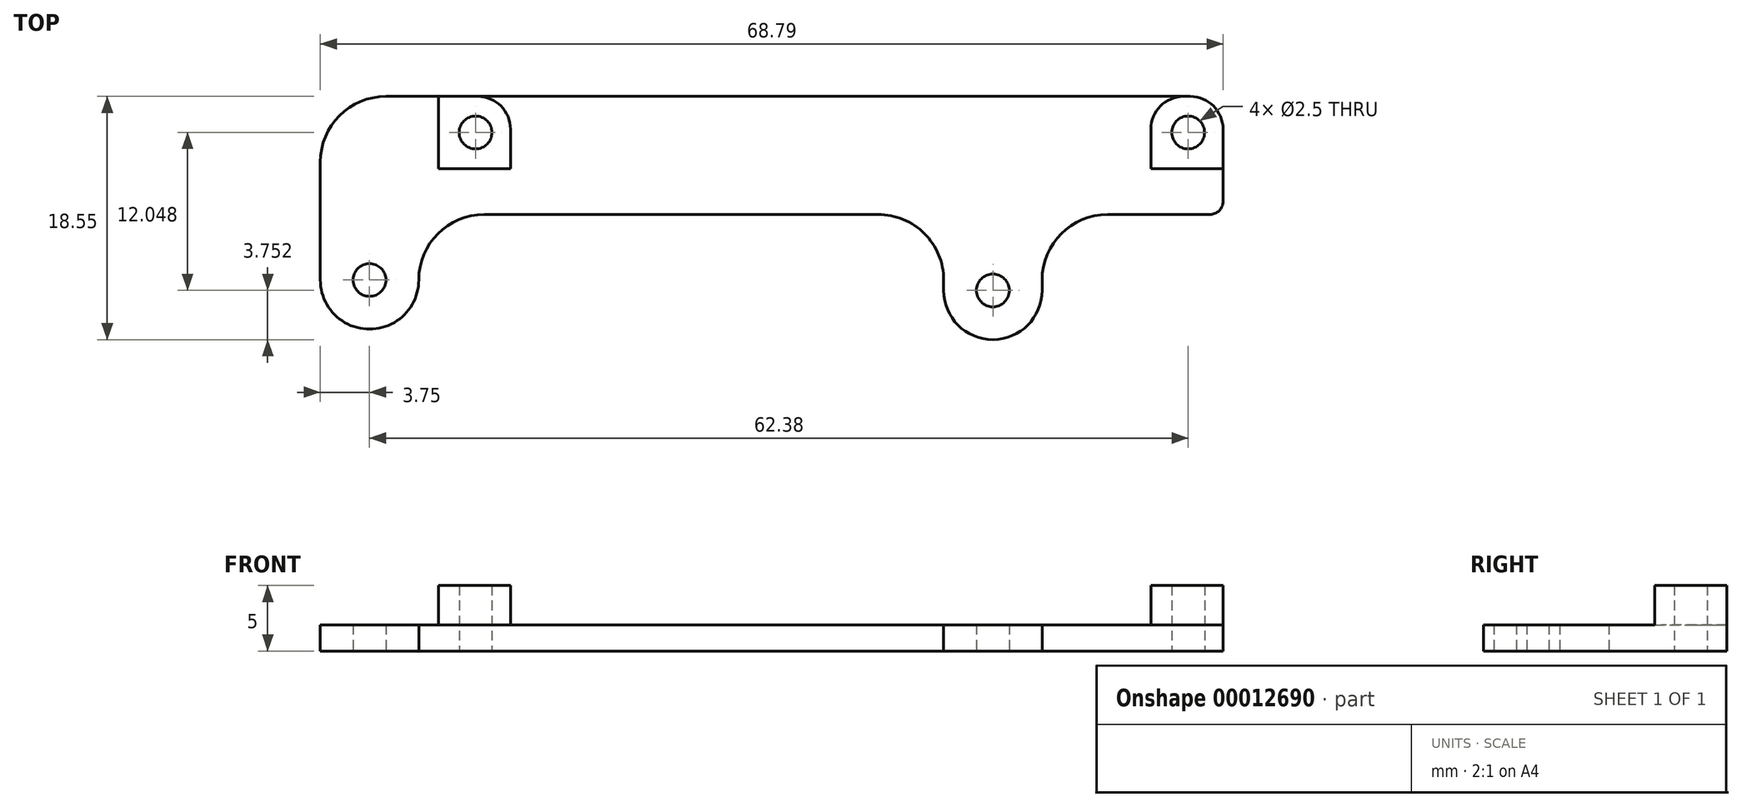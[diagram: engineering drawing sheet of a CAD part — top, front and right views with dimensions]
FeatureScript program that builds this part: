
annotation { "Feature Type Name" : "Feature", "Feature Type Description" : "" }
export const myFeature = defineFeature(function(context is Context, id is Id, definition is map)
    precondition{}
    {
        {
            var Q0;
            Q0=qCreatedBy(makeId("Top.planeOp"),FACE);
            var sketch = newSketch(context, id + "F0", { "sketchPlane" : qUnion([Q0])});
            skCircle(sketch, "E0", {"center": v(4.96, 27.14) * mm, "radius": 1.25 * mm});
            skCircle(sketch, "E1", {"center": v(-42.54, 27.94) * mm, "radius": 1.25 * mm});
            skArc(sketch, "E2.0", {"start": v(-46.3, 27.94) * mm, "mid": v(-42.54, 24.2) * mm, "end": v(-38.8, 27.94) * mm});
            skLineSegment(sketch, "E3", {"start": v(-46.3, 27.94) * mm, "end": v(-46.3, 36.94) * mm});
            skLineSegment(sketch, "E4", {"start": v(-38.8, 27.94) * mm, "end": v(-38.8, 27.94) * mm});
            skLineSegment(sketch, "E5", {"start": v(-33.8, 32.94) * mm, "end": v(-3.8, 32.94) * mm});
            skLineSegment(sketch, "E6", {"start": v(-41.3, 41.94) * mm, "end": v(20, 41.94) * mm});
            skPoint(sketch, "E7.visualSharp", {"position": v(-46.3, 41.94) * mm});
            skArc(sketch, "E7.filletArc", {"start": v(-41.3, 41.94) * mm, "mid": v(-44.83, 40.48) * mm, "end": v(-46.3, 36.94) * mm});
            skPoint(sketch, "E8.visualSharp", {"position": v(8.7, 41.94) * mm});
            skPoint(sketch, "E9.visualSharp", {"position": v(1.2, 32.94) * mm});
            skArc(sketch, "E9.filletArc", {"start": v(1.2, 27.94) * mm, "mid": v(-0.25, 31.48) * mm, "end": v(-3.8, 32.94) * mm});
            skPoint(sketch, "E10.visualSharp", {"position": v(-38.8, 32.94) * mm});
            skArc(sketch, "E10.filletArc", {"start": v(-33.8, 32.94) * mm, "mid": v(-37.33, 31.48) * mm, "end": v(-38.8, 27.94) * mm});
            skLineSegment(sketch, "E11", {"start": v(22.5, 39.44) * mm, "end": v(22.5, 33.93) * mm});
            skLineSegment(sketch, "E12.trimOffspring", {"start": v(13.7, 32.94) * mm, "end": v(21.5, 32.94) * mm});
            skPoint(sketch, "E13.visualSharp", {"position": v(8.7, 32.94) * mm});
            skArc(sketch, "E13.filletArc", {"start": v(13.7, 32.94) * mm, "mid": v(10.17, 31.48) * mm, "end": v(8.7, 27.94) * mm});
            skPoint(sketch, "E14.visualSharp", {"position": v(22.5, 32.94) * mm});
            skArc(sketch, "E14.filletArc", {"start": v(21.5, 32.94) * mm, "mid": v(22.21, 33.23) * mm, "end": v(22.5, 33.93) * mm});
            skPoint(sketch, "E15.visualSharp", {"position": v(22.5, 41.94) * mm});
            skArc(sketch, "E15.filletArc", {"start": v(22.5, 39.44) * mm, "mid": v(21.77, 41.2) * mm, "end": v(20, 41.94) * mm});
            skLineSegment(sketch, "E16", {"start": v(1.2, 27.94) * mm, "end": v(1.2, 27.14) * mm});
            skLineSegment(sketch, "E17", {"start": v(8.7, 27.94) * mm, "end": v(8.7, 27.14) * mm});
            skArc(sketch, "E18.0", {"start": v(1.2, 27.14) * mm, "mid": v(4.96, 23.4) * mm, "end": v(8.7, 27.14) * mm});
            skSolve(sketch);
        }
        {
            var Q0;
            Q0=makeQuery(id+"F0.imprint","IMPRINT",FACE,{"disambiguationData":[TD([[makeQuery(id+"F0.imprint","IMPRINT",EDGE,{"derivedFrom":sQuery(id+"F0.wireOp",EDGE,"E0")}),-1.0]])]});
            extrude(context, id + "F1", {"entities" : qUnion([Q0]), "depth" : 2 * mm});
        }
        {
            var Q0;
            Q0=makeQuery(id+"F1.opExtrude","CAP_FACE",FACE,{"disambiguationData":[OSD([sQuery(id+"F0.wireOp",EDGE,"E0"),sQuery(id+"F0.wireOp",EDGE,"45c87b56-47b0-4132-a54d-28034f3de5ed.0"),sQuery(id+"F0.wireOp",EDGE,"E1"),sQuery(id+"F0.wireOp",EDGE,"E2.0"),sQuery(id+"F0.wireOp",EDGE,"ccc7a8c6-e789-46e1-97a5-7ef8c04478ea"),sQuery(id+"F0.wireOp",EDGE,"ff894f09-860f-4312-a0db-dedd2cad3a32"),sQuery(id+"F0.wireOp",EDGE,"E3"),sQuery(id+"F0.wireOp",EDGE,"E4"),sQuery(id+"F0.wireOp",EDGE,"E5"),sQuery(id+"F0.wireOp",EDGE,"E6"),sQuery(id+"F0.wireOp",EDGE,"E7.filletArc"),sQuery(id+"F0.wireOp",EDGE,"E8.filletArc"),sQuery(id+"F0.wireOp",EDGE,"E9.filletArc"),sQuery(id+"F0.wireOp",EDGE,"E10.filletArc")])],"isStart":false});
            var sketch = newSketch(context, id + "F2", { "sketchPlane" : qUnion([Q0])});
            skLineSegment(sketch, "E19", {"start": v(-37.3, 36.44) * mm, "end": v(-37.3, 41.94) * mm});
            skLineSegment(sketch, "E20", {"start": v(-31.8, 36.44) * mm, "end": v(-31.8, 39.44) * mm});
            skLineSegment(sketch, "E21", {"start": v(-37.3, 36.44) * mm, "end": v(-31.8, 36.44) * mm});
            skCircle(sketch, "E22", {"center": v(-34.46, 39.2) * mm, "radius": 1.25 * mm});
            skLineSegment(sketch, "E23", {"start": v(-37.3, 41.94) * mm, "end": v(-34.3, 41.94) * mm});
            skCircle(sketch, "E24.1.0.0", {"center": v(19.84, 39.2) * mm, "radius": 1.25 * mm});
            skLineSegment(sketch, "E24.1.0.1", {"start": v(19.5, 41.94) * mm, "end": v(20, 41.94) * mm});
            skLineSegment(sketch, "E24.1.0.2", {"start": v(17, 36.44) * mm, "end": v(22.5, 36.44) * mm});
            skLineSegment(sketch, "E24.1.0.3", {"start": v(22.5, 36.44) * mm, "end": v(22.5, 39.44) * mm});
            skLineSegment(sketch, "E24.1.0.4", {"start": v(17, 36.44) * mm, "end": v(17, 39.44) * mm});
            skLineSegment(sketch, "E24.direction1", {"start": v(-34.46, 39.2) * mm, "end": v(19.84, 39.2) * mm, "construction": true});
            skPoint(sketch, "E25.visualSharp", {"position": v(22.5, 41.94) * mm});
            skArc(sketch, "E25.filletArc", {"start": v(22.5, 39.44) * mm, "mid": v(21.77, 41.2) * mm, "end": v(20, 41.94) * mm});
            skPoint(sketch, "E26.visualSharp", {"position": v(-31.8, 41.94) * mm});
            skArc(sketch, "E26.filletArc", {"start": v(-31.8, 39.44) * mm, "mid": v(-32.53, 41.2) * mm, "end": v(-34.3, 41.94) * mm});
            skPoint(sketch, "E27.visualSharp", {"position": v(17, 41.94) * mm});
            skArc(sketch, "E27.filletArc", {"start": v(19.5, 41.94) * mm, "mid": v(17.73, 41.2) * mm, "end": v(17, 39.44) * mm});
            skSolve(sketch);
        }
        {
            var Q0;
            Q0 = qSketchRegion(id + "F2", true);
            extrude(context, id + "F3", {"entities" : qUnion([Q0]), "operationType" : NewBodyOperationType.ADD, "depth" : 3 * mm});
        }
        {
            var Q0;
            Q0=sQuery(id+"F2.wireOp",VERTEX,"E24.direction1.start");
            var Q1;
            Q1=sQuery(id+"F2.wireOp",VERTEX,"E24.direction1.end");
            var Q2;
            Q2=makeQuery(id+"F1.opExtrude","SWEPT_BODY",BODY,{"disambiguationData":[OSD([sQuery(id+"F0.wireOp",EDGE,"E0"),sQuery(id+"F0.wireOp",EDGE,"45c87b56-47b0-4132-a54d-28034f3de5ed.0"),sQuery(id+"F0.wireOp",EDGE,"E1"),sQuery(id+"F0.wireOp",EDGE,"E2.0"),sQuery(id+"F0.wireOp",EDGE,"ccc7a8c6-e789-46e1-97a5-7ef8c04478ea"),sQuery(id+"F0.wireOp",EDGE,"ff894f09-860f-4312-a0db-dedd2cad3a32"),sQuery(id+"F0.wireOp",EDGE,"E3"),sQuery(id+"F0.wireOp",EDGE,"E4"),sQuery(id+"F0.wireOp",EDGE,"E5"),sQuery(id+"F0.wireOp",EDGE,"E6"),sQuery(id+"F0.wireOp",EDGE,"E7.filletArc"),sQuery(id+"F0.wireOp",EDGE,"E9.filletArc"),sQuery(id+"F0.wireOp",EDGE,"E10.filletArc"),sQuery(id+"F0.wireOp",EDGE,"2ba78112-90ed-48e8-a12f-9d0e51d58b7f"),sQuery(id+"F0.wireOp",EDGE,"604bb141-e0b2-4749-a987-c5a0c7516c7f"),sQuery(id+"F0.wireOp",EDGE,"e29db822-b3a0-42dd-a01a-dbbf7cf5480c"),sQuery(id+"F0.wireOp",EDGE,"E11"),sQuery(id+"F0.wireOp",EDGE,"E12.trimOffspring"),sQuery(id+"F0.wireOp",EDGE,"E13.filletArc"),sQuery(id+"F0.wireOp",EDGE,"E14.filletArc"),sQuery(id+"F0.wireOp",EDGE,"5d10bf31-ac50-4337-bbf5-15d5650545b1.filletArc")])]});
            hole(context, id + "F4", {"style" : HoleStyle.SIMPLE, "holeDiameter" : 2.5 * mm, "endStyle" : HoleEndStyle.THROUGH, "locations" : qUnion([Q0, Q1]), "scope" : qUnion([Q2])});
        }
    });
